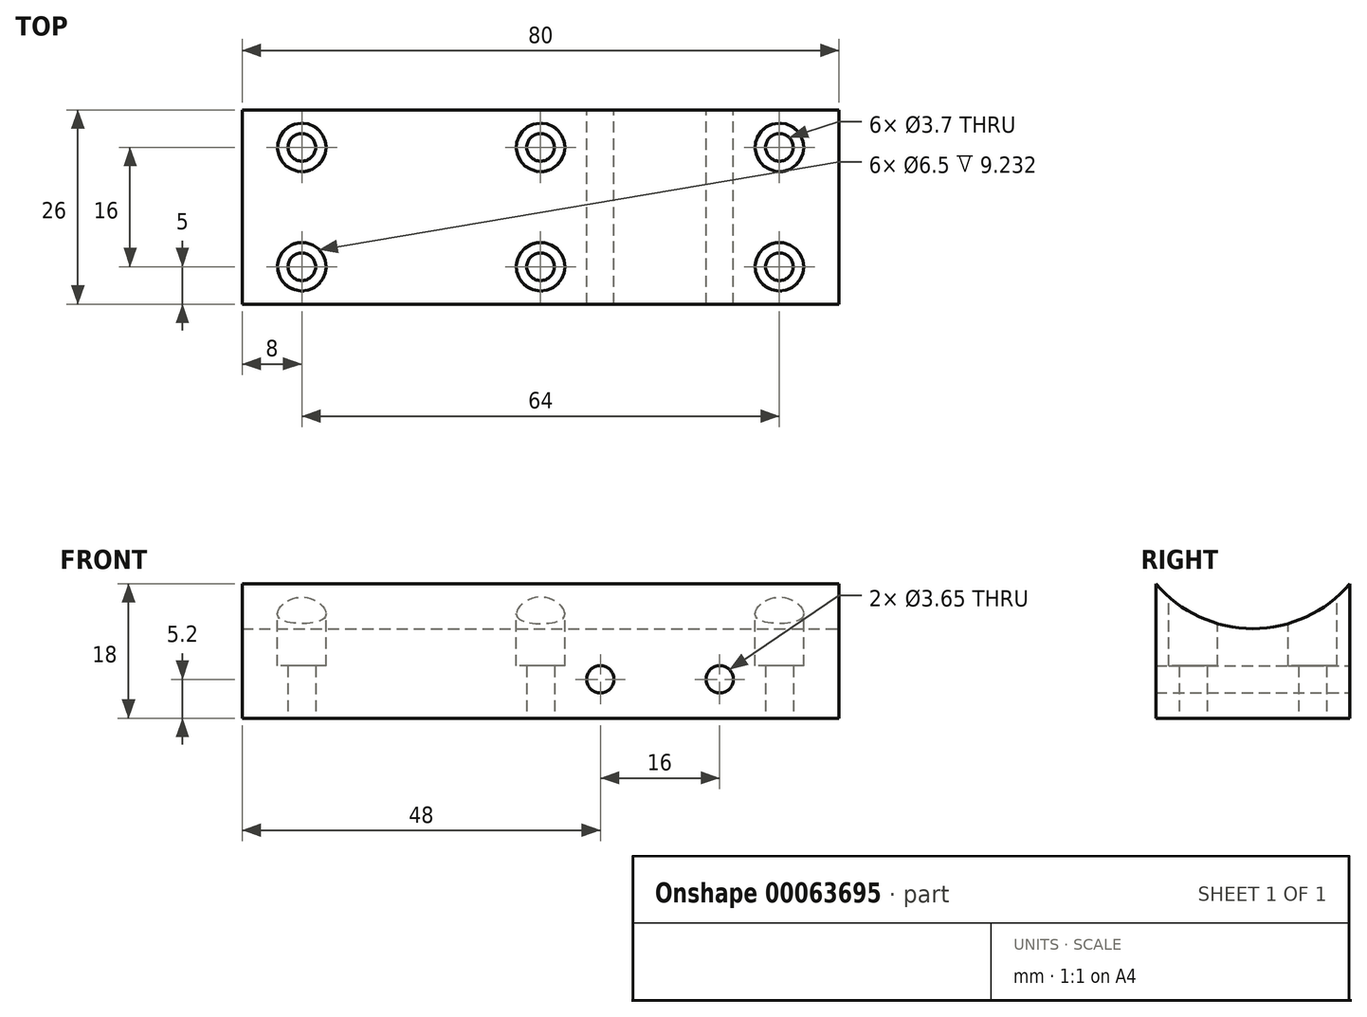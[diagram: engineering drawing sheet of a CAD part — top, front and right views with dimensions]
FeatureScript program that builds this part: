
annotation { "Feature Type Name" : "Feature", "Feature Type Description" : "" }
export const myFeature = defineFeature(function(context is Context, id is Id, definition is map)
    precondition{}
    {
        {
            var Q0;
            Q0=qCreatedBy(makeId("Top.planeOp"),FACE);
            var sketch = newSketch(context, id + "F0", { "sketchPlane" : qUnion([Q0])});
            skLineSegment(sketch, "E0.rect.bottom", {"start": v(-40, -13) * mm, "end": v(40, -13) * mm});
            skLineSegment(sketch, "E0.rect.top", {"start": v(-40, 13) * mm, "end": v(40, 13) * mm});
            skLineSegment(sketch, "E0.rect.left", {"start": v(-40, -13) * mm, "end": v(-40, 13) * mm});
            skLineSegment(sketch, "E0.rect.right", {"start": v(40, -13) * mm, "end": v(40, 13) * mm});
            skPoint(sketch, "E0.rect.middle", {"position": v(0, 0) * mm});
            skCircle(sketch, "E1", {"center": v(0, 8) * mm, "radius": 1.85 * mm});
            skCircle(sketch, "E2.2.0", {"center": v(0, -8) * mm, "radius": 1.85 * mm});
            skPoint(sketch, "E3.1.0.2", {"position": v(32, 0) * mm});
            skCircle(sketch, "E3.1.0.3", {"center": v(32, 8) * mm, "radius": 1.85 * mm});
            skPoint(sketch, "E3.1.0.5", {"position": v(32, 0) * mm});
            skCircle(sketch, "E3.1.0.6", {"center": v(32, -8) * mm, "radius": 1.85 * mm});
            skCircle(sketch, "E4.1.0.0", {"center": v(-32, 8) * mm, "radius": 1.85 * mm});
            skCircle(sketch, "E4.1.0.1", {"center": v(-32, -8) * mm, "radius": 1.85 * mm});
            skLineSegment(sketch, "E4.direction1", {"start": v(0, 8) * mm, "end": v(-32, 8) * mm, "construction": true});
            skSolve(sketch);
        }
        {
            var Q0;
            Q0=makeQuery(id+"F0.imprint","IMPRINT",FACE,{"disambiguationData":[TD([[makeQuery(id+"F0.imprint","IMPRINT",EDGE,{"derivedFrom":sQuery(id+"F0.wireOp",EDGE,"E0.rect.bottom")}),1.0]])]});
            extrude(context, id + "F1", {"entities" : qUnion([Q0]), "depth" : 25 * mm});
        }
        {
            var Q0;
            Q0=makeQuery(id+"F1.opExtrude","SWEPT_FACE",FACE,{"disambiguationData":[OSD([sQuery(id+"F0.wireOp",EDGE,"E0.rect.right")])]});
            var sketch = newSketch(context, id + "F2", { "sketchPlane" : qUnion([Q0])});
            skLineSegment(sketch, "E5", {"start": v(-13, 0) * mm, "end": v(-13, 18) * mm, "construction": true});
            skLineSegment(sketch, "E6", {"start": v(0, 0) * mm, "end": v(0, 12) * mm, "construction": true});
            skPoint(sketch, "E6.endSnap0", {"position": v(0, 0) * mm});
            skArc(sketch, "E7", {"start": v(-13, 18) * mm, "mid": v(0, 12) * mm, "end": v(13, 18) * mm});
            skSolve(sketch);
        }
        {
            var Q0;
            Q0=makeQuery(id+"F1.opExtrude","CAP_FACE",FACE,{"disambiguationData":[OSD([sQuery(id+"F0.wireOp",EDGE,"E0.rect.bottom"),sQuery(id+"F0.wireOp",EDGE,"E0.rect.top"),sQuery(id+"F0.wireOp",EDGE,"E0.rect.left"),sQuery(id+"F0.wireOp",EDGE,"E0.rect.right"),sQuery(id+"F0.wireOp",EDGE,"E1"),sQuery(id+"F0.wireOp",EDGE,"E2.2.0"),sQuery(id+"F0.wireOp",EDGE,"E3.1.0.3"),sQuery(id+"F0.wireOp",EDGE,"E3.1.0.6"),sQuery(id+"F0.wireOp",EDGE,"E4.1.0.0"),sQuery(id+"F0.wireOp",EDGE,"E4.1.0.1")])],"isStart":false});
            var sketch = newSketch(context, id + "F3", { "sketchPlane" : qUnion([Q0])});
            skCircle(sketch, "E8", {"center": v(-32, 8) * mm, "radius": 3.25 * mm});
            skCircle(sketch, "E9", {"center": v(-32, -8) * mm, "radius": 3.25 * mm});
            skCircle(sketch, "E10.1.0.0", {"center": v(0, 8) * mm, "radius": 3.25 * mm});
            skCircle(sketch, "E10.1.0.1", {"center": v(0, -8) * mm, "radius": 3.25 * mm});
            skCircle(sketch, "E10.2.0.0", {"center": v(32, 8) * mm, "radius": 3.25 * mm});
            skCircle(sketch, "E10.2.0.1", {"center": v(32, -8) * mm, "radius": 3.25 * mm});
            skLineSegment(sketch, "E10.direction1", {"start": v(-32, 8) * mm, "end": v(0, 8) * mm, "construction": true});
            skSolve(sketch);
        }
        {
            var Q0;
            Q0=makeQuery(id+"F3.imprint","IMPRINT",FACE,{"disambiguationData":[TD([[makeQuery(id+"F3.imprint","IMPRINT",EDGE,{"derivedFrom":sQuery(id+"F3.wireOp",EDGE,"E9")}),1.0]])]});
            var Q1;
            Q1=makeQuery(id+"F3.imprint","IMPRINT",FACE,{"disambiguationData":[TD([[makeQuery(id+"F3.imprint","IMPRINT",EDGE,{"derivedFrom":sQuery(id+"F3.wireOp",EDGE,"E8")}),1.0]])]});
            var Q2;
            Q2=makeQuery(id+"F3.imprint","IMPRINT",FACE,{"disambiguationData":[TD([[makeQuery(id+"F3.imprint","IMPRINT",EDGE,{"derivedFrom":sQuery(id+"F3.wireOp",EDGE,"E10.1.0.0")}),1.0]])]});
            var Q3;
            Q3=makeQuery(id+"F3.imprint","IMPRINT",FACE,{"disambiguationData":[TD([[makeQuery(id+"F3.imprint","IMPRINT",EDGE,{"derivedFrom":sQuery(id+"F3.wireOp",EDGE,"E10.1.0.1")}),1.0]])]});
            var Q4;
            Q4=makeQuery(id+"F3.imprint","IMPRINT",FACE,{"disambiguationData":[TD([[makeQuery(id+"F3.imprint","IMPRINT",EDGE,{"derivedFrom":sQuery(id+"F3.wireOp",EDGE,"E10.2.0.0")}),1.0]])]});
            var Q5;
            Q5=makeQuery(id+"F3.imprint","IMPRINT",FACE,{"disambiguationData":[TD([[makeQuery(id+"F3.imprint","IMPRINT",EDGE,{"derivedFrom":sQuery(id+"F3.wireOp",EDGE,"E10.2.0.1")}),1.0]])]});
            extrude(context, id + "F4", {"entities" : qUnion([Q0, Q1, Q2, Q3, Q4, Q5]), "operationType" : NewBodyOperationType.REMOVE, "oppositeDirection" : true, "depth" : 18 * mm});
        }
        {
            var Q0;
            {var subQ0=sQuery(id+"F2.wireOp",EDGE,"E7");Q0=makeQuery(id+"F2.imprint","IMPRINT",FACE,{"disambiguationData":[TD([[makeQuery(id+"F2.imprint","IMPRINT",EDGE,{"derivedFrom":subQ0}),1.0]])]});}
            extrude(context, id + "F5", {"entities" : qUnion([Q0]), "operationType" : NewBodyOperationType.REMOVE, "oppositeDirection" : true, "depth" : 100 * mm});
        }
        {
            var Q0;
            Q0=makeQuery(id+"F1.opExtrude","SWEPT_FACE",FACE,{"disambiguationData":[OSD([sQuery(id+"F0.wireOp",EDGE,"E0.rect.top")])]});
            var sketch = newSketch(context, id + "F6", { "sketchPlane" : qUnion([Q0])});
            skLineSegment(sketch, "E11", {"start": v(0, 18) * mm, "end": v(0, 5.2) * mm, "construction": true});
            skPoint(sketch, "E11.endSnap0", {"position": v(0, 18) * mm});
            skLineSegment(sketch, "E12", {"start": v(0, 5.2) * mm, "end": v(-8, 5.2) * mm, "construction": true});
            skCircle(sketch, "E13", {"center": v(-8, 5.2) * mm, "radius": 1.83 * mm});
            skLineSegment(sketch, "E14", {"start": v(-8, 5.2) * mm, "end": v(-24, 5.2) * mm, "construction": true});
            skCircle(sketch, "E15", {"center": v(-24, 5.2) * mm, "radius": 1.82 * mm});
            skSolve(sketch);
        }
        {
            var Q0;
            Q0=makeQuery(id+"F6.imprint","IMPRINT",FACE,{"disambiguationData":[TD([[makeQuery(id+"F6.imprint","IMPRINT",EDGE,{"derivedFrom":sQuery(id+"F6.wireOp",EDGE,"E15")}),1.0]])]});
            var Q1;
            Q1=makeQuery(id+"F6.imprint","IMPRINT",FACE,{"disambiguationData":[TD([[makeQuery(id+"F6.imprint","IMPRINT",EDGE,{"derivedFrom":sQuery(id+"F6.wireOp",EDGE,"E13")}),1.0]])]});
            extrude(context, id + "F7", {"entities" : qUnion([Q0, Q1]), "operationType" : NewBodyOperationType.REMOVE, "oppositeDirection" : true, "depth" : 90 * mm});
        }
    });
